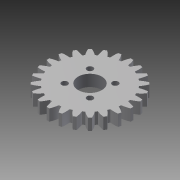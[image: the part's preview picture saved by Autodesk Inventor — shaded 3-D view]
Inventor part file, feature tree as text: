
AUTODESK INVENTOR PART (.ipt)
format: ipt  version: 2014 (Build 180170000, 170)  size: 284,160 bytes
history: native  units: mm
features: other x4, extrude x3, sketch x3
ambient origin geometry x8: Origin, YZ Plane, XZ Plane, XY Plane, X Axis, Y Axis, Z Axis, Center Point
bodies: Body1 (feature_tree)
feature tree (10):
  other  "平歯車1"
  extrude  "押し出し1"  Depth=10.0mm
  extrude  "押し出し2"  Depth=8.2mm
  extrude  "押し出し3"  Depth=10.0mm TaperAngle=0.0deg
  other  "Solid1::平歯車1"
  other  "TaggingFeature1"
  sketch  "スケッチ1"
  sketch  "スケッチ2"
  sketch  "スケッチ3"
  other  "ソリッド1"
